# Revit family: FPL2-EQ0595xxWS8X0840MPS0400
name_source: partatom
category: Leuchten
units: mm (PartAtom-declared; Revit-internal decimal feet)

## family parameters
Basisbauteil = Fläche
Beim Laden mit Abzugskörper schneiden = Nein
Bemaßung runder Anschluss = Durchmesser verwenden
Gemeinsam genutzt = Nein
Lichtquelle = Ja
OmniClass-Nummer = 23.80.70.11
OmniClass-Titel = Luminaries for Internal Lighting
Raumberechnungspunkt = Nein
Teiletyp = Normal

## types (4) — shared parameters
Baugruppenkennzeichen = D5020200
Datei für fotometrisches Netz = FPL2-EQ0595.IES
Emissionsform beim Rendern sichtbar = Nein
Farbfilter = 16777215
Farbtemperaturverschiebung bei Dämpfen der Lampe = <Keine Auswahl>
Hersteller = RIDI Leuchten GmbH
Lampe = LED
Neigungswinkel = 90.00°
Scheinlast = 33 VA
URL = www.ridi.de
Von Breite des Rechtecks ausssenden = 545 mm  [stored 1.78806 ft]
Von Länge des Rechtecks aussenden = 545 mm  [stored 1.78806 ft]
brand = RIDI
conformity mark = CE
electrical safety class = 1
height = 15 mm  [stored 0.0492126 ft]
ingress protection (IP) code = IP40
length = 620 mm  [stored 2.03412 ft]
nominal frequency = 50-60Hz
nominal voltage = 230
rated input power = 33
voltage type (AC, DC, UC) = AC
width = 620 mm  [stored 2.03412 ft]
zero-valued in all types: Vorgabe-Ansicht

## per-type parameters (varying)
| type | Modell | weight |
| FPL2-EQ0595DAWS830840MPS0400 | 0832975 | 2.1 kg |
| FPL2-EQ0595NDWS830840MPS0400 | 0822975 | 2.1 kg |
| FPL2-EQ0595NDWS850865MPS0400 | 0822979 | 2.1 kg |
| FPL2-EQ0595DAWS850865MPS0400 | 0832979 | 2,1 kg |

note: column(s) folded — value = type name in every type: product name

note: [stored X ft] marks values corroborated as IEEE doubles in the binary element streams (Revit-internal decimal feet)
